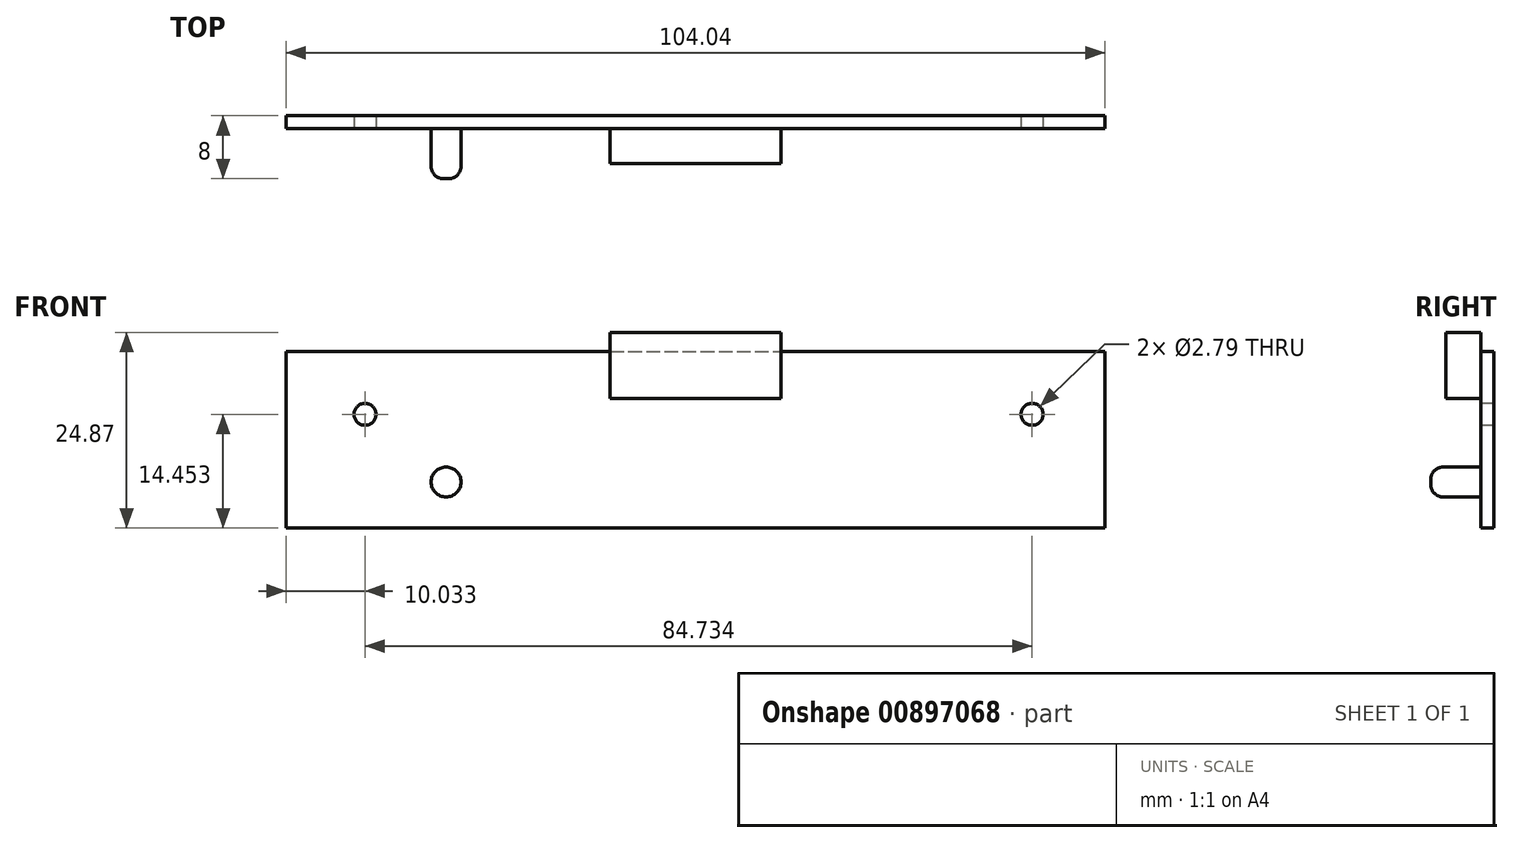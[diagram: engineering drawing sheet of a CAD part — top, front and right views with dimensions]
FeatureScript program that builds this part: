
annotation { "Feature Type Name" : "Feature", "Feature Type Description" : "" }
export const myFeature = defineFeature(function(context is Context, id is Id, definition is map)
    precondition{}
    {
        {
            var Q0;
            Q0=qCreatedBy(makeId("Front.planeOp"),FACE);
            var sketch = newSketch(context, id + "F0", { "sketchPlane" : qUnion([Q0])});
            skLineSegment(sketch, "E0.bottom", {"start": v(0, 0) * mm, "end": v(104.04, 0) * mm});
            skLineSegment(sketch, "E0.top", {"start": v(0, 22.45) * mm, "end": v(104.04, 22.45) * mm});
            skLineSegment(sketch, "E0.left", {"start": v(0, 0) * mm, "end": v(0, 22.45) * mm});
            skLineSegment(sketch, "E0.right", {"start": v(104.04, 0) * mm, "end": v(104.04, 22.45) * mm});
            skSolve(sketch);
        }
        {
            var Q0;
            Q0 = qSketchRegion(id + "F0", true);
            extrude(context, id + "F1", {"entities" : qUnion([Q0]), "depth" : 1.65 * mm, "offsetDistance" : 25.4 * mm});
        }
        {
            var Q0;
            Q0=makeQuery(id+"F1.opExtrude","CAP_FACE",FACE,{"disambiguationData":[OSD([sQuery(id+"F0.wireOp",EDGE,"E0.bottom"),sQuery(id+"F0.wireOp",EDGE,"E0.top"),sQuery(id+"F0.wireOp",EDGE,"E0.left"),sQuery(id+"F0.wireOp",EDGE,"E0.right")])],"isStart":false});
            var sketch = newSketch(context, id + "F2", { "sketchPlane" : qUnion([Q0])});
            skCircle(sketch, "E1", {"center": v(20.32, 5.84) * mm, "radius": 1.9 * mm});
            skSolve(sketch);
        }
        {
            var Q0;
            Q0 = qSketchRegion(id + "F2", true);
            extrude(context, id + "F3", {"entities" : qUnion([Q0]), "operationType" : NewBodyOperationType.ADD, "depth" : 6.35 * mm, "offsetDistance" : 25.4 * mm});
        }
        {
            var Q0;
            Q0=makeQuery(id+"F3.opExtrude","CAP_FACE",FACE,{"disambiguationData":[OSD([sQuery(id+"F2.wireOp",EDGE,"E1")])],"isStart":false});
            fillet(context, id + "F4", {"entities" : qUnion([Q0]), "radius" : 1.59 * mm, "tangentPropagation" : true, "allowEdgeOverflow" : false});
        }
        {
            var Q0;
            Q0=makeQuery(id+"F1.opExtrude","CAP_FACE",FACE,{"disambiguationData":[OSD([sQuery(id+"F0.wireOp",EDGE,"E0.bottom"),sQuery(id+"F0.wireOp",EDGE,"E0.top"),sQuery(id+"F0.wireOp",EDGE,"E0.left"),sQuery(id+"F0.wireOp",EDGE,"E0.right")])],"isStart":false});
            var sketch = newSketch(context, id + "F5", { "sketchPlane" : qUnion([Q0])});
            skCircle(sketch, "E2", {"center": v(10.03, 14.45) * mm, "radius": 1.4 * mm});
            skCircle(sketch, "E3", {"center": v(94.77, 14.45) * mm, "radius": 1.4 * mm});
            skSolve(sketch);
        }
        {
            var Q0;
            Q0 = qSketchRegion(id + "F5", true);
            extrude(context, id + "F6", {"entities" : qUnion([Q0]), "operationType" : NewBodyOperationType.REMOVE, "endBound" : BoundingType.UP_TO_NEXT, "oppositeDirection" : true, "depth" : 25.4 * mm, "offsetDistance" : 25.4 * mm});
        }
        {
            var Q0;
            Q0=makeQuery(id+"F1.opExtrude","CAP_FACE",FACE,{"disambiguationData":[OSD([sQuery(id+"F0.wireOp",EDGE,"E0.bottom"),sQuery(id+"F0.wireOp",EDGE,"E0.top"),sQuery(id+"F0.wireOp",EDGE,"E0.left"),sQuery(id+"F0.wireOp",EDGE,"E0.right")])],"isStart":false});
            var sketch = newSketch(context, id + "F7", { "sketchPlane" : qUnion([Q0])});
            skLineSegment(sketch, "E4.bottom", {"start": v(41.16, 24.87) * mm, "end": v(62.88, 24.87) * mm});
            skLineSegment(sketch, "E4.top", {"start": v(41.16, 16.48) * mm, "end": v(62.88, 16.48) * mm});
            skLineSegment(sketch, "E4.left", {"start": v(41.16, 24.87) * mm, "end": v(41.16, 16.48) * mm});
            skLineSegment(sketch, "E4.right", {"start": v(62.88, 24.87) * mm, "end": v(62.88, 16.48) * mm});
            skPoint(sketch, "E5", {"position": v(52.02, 22.45) * mm});
            skPoint(sketch, "E6", {"position": v(52.02, 24.87) * mm});
            skSolve(sketch);
        }
        {
            var Q0;
            Q0 = qSketchRegion(id + "F7", true);
            extrude(context, id + "F8", {"entities" : qUnion([Q0]), "operationType" : NewBodyOperationType.ADD, "depth" : 4.44 * mm, "offsetDistance" : 25.4 * mm});
        }
    });
